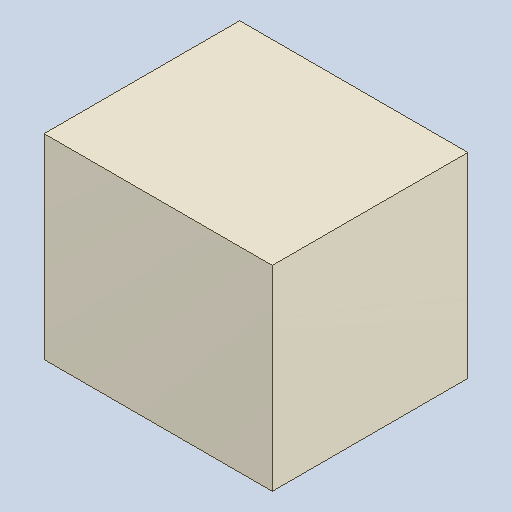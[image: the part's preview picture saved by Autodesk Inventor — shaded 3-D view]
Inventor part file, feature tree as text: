
AUTODESK INVENTOR PART (.ipt)
format: ipt  version: 2023.4 (Build 274418000, 418)  size: 82,432 bytes
history: native  units: mm
features: extrude x1
ambient origin geometry x8: Origin, YZ Plane, XZ Plane, XY Plane, X Axis, Y Axis, Z Axis, Center Point
bodies: Solid1 (feature_tree)
feature tree (1):
  extrude  "Extruded_17"  [1 undecoded]
note: 1 required parameter value undecoded (feature->parameter linkage not recoverable at this tier; creation-order binding heuristic only, values carry confidence <= 0.55)
